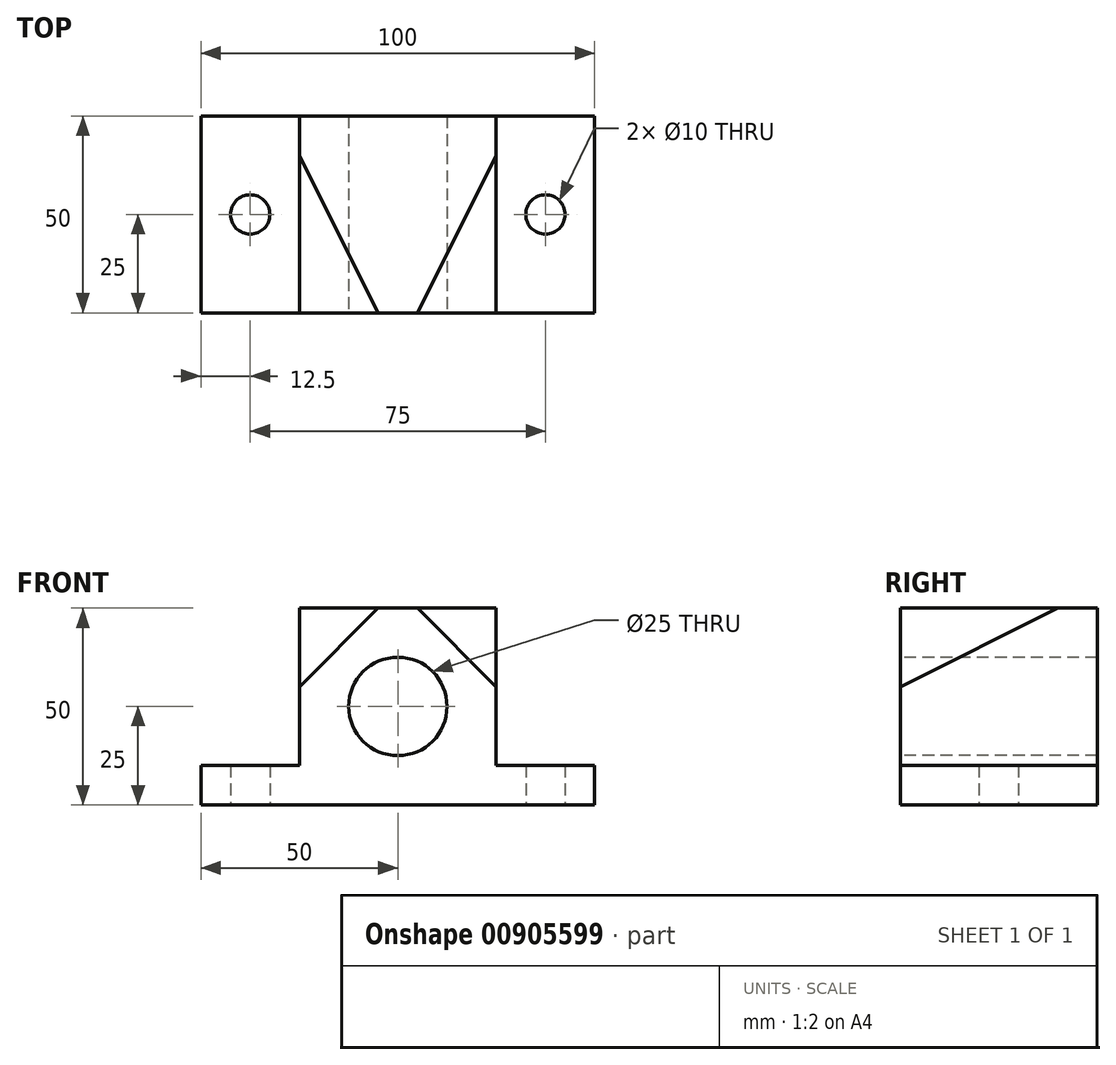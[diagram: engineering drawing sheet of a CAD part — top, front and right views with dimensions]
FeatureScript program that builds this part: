
annotation { "Feature Type Name" : "Feature", "Feature Type Description" : "" }
export const myFeature = defineFeature(function(context is Context, id is Id, definition is map)
    precondition{}
    {
        {
            var Q0;
            Q0=qCreatedBy(makeId("Top.planeOp"),FACE);
            var sketch = newSketch(context, id + "F0", { "sketchPlane" : qUnion([Q0])});
            skLineSegment(sketch, "E0", {"start": v(-73.6, 0) * mm, "end": v(76.3, 0) * mm, "construction": true});
            skLineSegment(sketch, "E1", {"start": v(0, 74.95) * mm, "end": v(0, -74.95) * mm, "construction": true});
            skLineSegment(sketch, "E2.bottom", {"start": v(50, 25) * mm, "end": v(-50, 25) * mm});
            skLineSegment(sketch, "E2.top", {"start": v(50, -25) * mm, "end": v(-50, -25) * mm});
            skLineSegment(sketch, "E2.left", {"start": v(50, 25) * mm, "end": v(50, -25) * mm});
            skLineSegment(sketch, "E2.right", {"start": v(-50, 25) * mm, "end": v(-50, -25) * mm});
            skPoint(sketch, "E2.middle", {"position": v(0, 0) * mm});
            skSolve(sketch);
        }
        {
            var Q0;
            Q0=makeQuery(id+"F0.imprint","IMPRINT",FACE,{"disambiguationData":[TD([[makeQuery(id+"F0.imprint","IMPRINT",EDGE,{"derivedFrom":sQuery(id+"F0.wireOp",EDGE,"E2.bottom")}),1.0]])]});
            extrude(context, id + "F1", {"entities" : qUnion([Q0]), "depth" : 50 * mm, "offsetDistance" : 25 * mm});
        }
        {
            var Q0;
            Q0=makeQuery(id+"F1.opExtrude","SWEPT_FACE",FACE,{"disambiguationData":[OSD([sQuery(id+"F0.wireOp",EDGE,"E2.top")])]});
            var sketch = newSketch(context, id + "F2", { "sketchPlane" : qUnion([Q0])});
            skLineSegment(sketch, "E3.0", {"start": v(-25, 25) * mm, "end": v(25, 25) * mm, "construction": true});
            skLineSegment(sketch, "E3.1", {"start": v(-25, 25) * mm, "end": v(-25, 25) * mm});
            skLineSegment(sketch, "E3.3", {"start": v(25, 25) * mm, "end": v(25, 25) * mm});
            skLineSegment(sketch, "E4", {"start": v(0, 66.46) * mm, "end": v(0, -21.33) * mm, "construction": true});
            skCircle(sketch, "E5", {"center": v(0, 25) * mm, "radius": 12.5 * mm});
            skSolve(sketch);
        }
        {
            var Q0;
            Q0=makeQuery(id+"F2.imprint","IMPRINT",FACE,{"disambiguationData":[TD([[makeQuery(id+"F2.imprint","IMPRINT",EDGE,{"derivedFrom":sQuery(id+"F2.wireOp",EDGE,"E5")}),1.0]])]});
            extrude(context, id + "F3", {"entities" : qUnion([Q0]), "operationType" : NewBodyOperationType.REMOVE, "endBound" : BoundingType.THROUGH_ALL, "oppositeDirection" : true, "depth" : 25 * mm, "offsetDistance" : 25 * mm});
        }
        {
            var Q0;
            Q0=makeQuery(id+"F1.opExtrude","SWEPT_FACE",FACE,{"disambiguationData":[OSD([sQuery(id+"F0.wireOp",EDGE,"E2.top")])]});
            var sketch = newSketch(context, id + "F4", { "sketchPlane" : qUnion([Q0])});
            skLineSegment(sketch, "E6.bottom", {"start": v(-50, 50) * mm, "end": v(-25, 50) * mm});
            skLineSegment(sketch, "E6.top", {"start": v(-50, 10) * mm, "end": v(-25, 10) * mm});
            skLineSegment(sketch, "E6.left", {"start": v(-50, 50) * mm, "end": v(-50, 10) * mm});
            skLineSegment(sketch, "E6.right", {"start": v(-25, 50) * mm, "end": v(-25, 10) * mm});
            skLineSegment(sketch, "E7.MirrorCS", {"start": v(25, 50) * mm, "end": v(25, 10) * mm});
            skLineSegment(sketch, "E8.MirrorCS", {"start": v(50, 50) * mm, "end": v(25, 50) * mm});
            skLineSegment(sketch, "E9.MirrorCS", {"start": v(50, 50) * mm, "end": v(50, 10) * mm});
            skLineSegment(sketch, "E10.MirrorCS", {"start": v(50, 10) * mm, "end": v(25, 10) * mm});
            skSolve(sketch);
        }
        {
            var Q0;
            Q0=makeQuery(id+"F4.imprint","IMPRINT",FACE,{"disambiguationData":[TD([[makeQuery(id+"F4.imprint","IMPRINT",EDGE,{"derivedFrom":sQuery(id+"F4.wireOp",EDGE,"E6.bottom")}),1.0]])]});
            var Q1;
            Q1=makeQuery(id+"F4.imprint","IMPRINT",FACE,{"disambiguationData":[TD([[makeQuery(id+"F4.imprint","IMPRINT",EDGE,{"derivedFrom":sQuery(id+"F4.wireOp",EDGE,"E7.MirrorCS")}),1.0]])]});
            extrude(context, id + "F5", {"entities" : qUnion([Q0, Q1]), "operationType" : NewBodyOperationType.REMOVE, "endBound" : BoundingType.THROUGH_ALL, "oppositeDirection" : true, "depth" : 25 * mm, "offsetDistance" : 25 * mm});
        }
        {
            var Q0;
            Q0=makeQuery(id+"F1.opExtrude","CAP_FACE",FACE,{"disambiguationData":[OSD([sQuery(id+"F0.wireOp",EDGE,"E2.bottom"),sQuery(id+"F0.wireOp",EDGE,"E2.top"),sQuery(id+"F0.wireOp",EDGE,"E2.left"),sQuery(id+"F0.wireOp",EDGE,"E2.right")])],"isStart":true});
            var sketch = newSketch(context, id + "F6", { "sketchPlane" : qUnion([Q0])});
            skLineSegment(sketch, "E11", {"start": v(-73.99, 0) * mm, "end": v(76.67, 0) * mm, "construction": true});
            skPoint(sketch, "E11.endSnap0", {"position": v(50, 0) * mm});
            skLineSegment(sketch, "E12", {"start": v(0, 63.25) * mm, "end": v(0, -70.97) * mm, "construction": true});
            skLineSegment(sketch, "E13.0", {"start": v(-37.5, -25) * mm, "end": v(-37.5, 25) * mm, "construction": true});
            skLineSegment(sketch, "E14.0", {"start": v(37.5, -25) * mm, "end": v(37.5, 25) * mm, "construction": true});
            skCircle(sketch, "E15", {"center": v(-37.5, 0) * mm, "radius": 5 * mm});
            skCircle(sketch, "E16", {"center": v(37.5, 0) * mm, "radius": 5 * mm});
            skSolve(sketch);
        }
        {
            var Q0;
            Q0=makeQuery(id+"F6.imprint","IMPRINT",FACE,{"disambiguationData":[TD([[makeQuery(id+"F6.imprint","IMPRINT",EDGE,{"derivedFrom":sQuery(id+"F6.wireOp",EDGE,"E15")}),1.0]])]});
            var Q1;
            Q1=makeQuery(id+"F6.imprint","IMPRINT",FACE,{"disambiguationData":[TD([[makeQuery(id+"F6.imprint","IMPRINT",EDGE,{"derivedFrom":sQuery(id+"F6.wireOp",EDGE,"E16")}),1.0]])]});
            extrude(context, id + "F7", {"entities" : qUnion([Q0, Q1]), "operationType" : NewBodyOperationType.REMOVE, "endBound" : BoundingType.THROUGH_ALL, "oppositeDirection" : true, "depth" : 25 * mm, "offsetDistance" : 25 * mm});
        }
        {
            var Q0;
            Q0=makeQuery(id+"F1.opExtrude","SWEPT_FACE",FACE,{"disambiguationData":[OSD([sQuery(id+"F0.wireOp",EDGE,"E2.top")])]});
            var sketch = newSketch(context, id + "F8", { "sketchPlane" : qUnion([Q0])});
            skLineSegment(sketch, "E17", {"start": v(5, 50) * mm, "end": v(25, 50) * mm});
            skLineSegment(sketch, "E18", {"start": v(25, 50) * mm, "end": v(25, 30) * mm});
            skLineSegment(sketch, "E19", {"start": v(25, 30) * mm, "end": v(5, 50) * mm});
            skSolve(sketch);
        }
        {
            var Q0;
            Q0=makeQuery(id+"F1.opExtrude","CAP_FACE",FACE,{"disambiguationData":[OSD([sQuery(id+"F0.wireOp",EDGE,"E2.bottom"),sQuery(id+"F0.wireOp",EDGE,"E2.top"),sQuery(id+"F0.wireOp",EDGE,"E2.left"),sQuery(id+"F0.wireOp",EDGE,"E2.right")])],"isStart":false});
            var sketch = newSketch(context, id + "F9", { "sketchPlane" : qUnion([Q0])});
            skLineSegment(sketch, "E20", {"start": v(25, -25) * mm, "end": v(5, -25) * mm});
            skLineSegment(sketch, "E21", {"start": v(5, -25) * mm, "end": v(25, 15) * mm});
            skLineSegment(sketch, "E22", {"start": v(25, 15) * mm, "end": v(25, -25) * mm});
            skSolve(sketch);
        }
        {
            var Q0;
            Q0=sQuery(id+"F8.wireOp",VERTEX,"E17.start");
            var Q1;
            Q1=sQuery(id+"F8.wireOp",VERTEX,"E18.end");
            var Q2;
            Q2=sQuery(id+"F9.wireOp",VERTEX,"E21.end");
            cPlane(context, id + "F10", {"entities" : qUnion([Q0, Q1, Q2]), "cplaneType" : CPlaneType.THREE_POINT, "offset" : 25 * mm, "width" : 150 * mm, "height" : 150 * mm});
        }
        {
            var Q0;
            Q0=qCreatedBy(id+"F10.planeOp",FACE);
            var Q1;
            Q1=sQuery(id+"F8.wireOp",VERTEX,"E17.end");
            cPlane(context, id + "F11", {"entities" : qUnion([Q0, Q1]), "cplaneType" : CPlaneType.PLANE_POINT, "offset" : 25 * mm, "width" : 150 * mm, "height" : 150 * mm});
        }
        {
            var Q0;
            Q0=qCreatedBy(id+"F11.planeOp",FACE);
            var sketch = newSketch(context, id + "F12", { "sketchPlane" : qUnion([Q0])});
            skLineSegment(sketch, "E23.bottom", {"start": v(22.63, 47.37) * mm, "end": v(-40.66, 47.37) * mm});
            skLineSegment(sketch, "E23.top", {"start": v(22.63, -18.36) * mm, "end": v(-40.66, -18.36) * mm});
            skLineSegment(sketch, "E23.left", {"start": v(22.63, 47.37) * mm, "end": v(22.63, -18.36) * mm});
            skLineSegment(sketch, "E23.right", {"start": v(-40.66, 47.37) * mm, "end": v(-40.66, -18.36) * mm});
            skSolve(sketch);
        }
        {
            var Q0;
            Q0=makeQuery(id+"F12.imprint","IMPRINT",FACE,{"disambiguationData":[TD([[makeQuery(id+"F12.imprint","IMPRINT",EDGE,{"derivedFrom":sQuery(id+"F12.wireOp",EDGE,"E23.bottom")}),1.0]])]});
            var Q1;
            Q1=qCreatedBy(id+"F10.planeOp",FACE);
            extrude(context, id + "F13", {"entities" : qUnion([Q0]), "operationType" : NewBodyOperationType.REMOVE, "endBound" : BoundingType.UP_TO_SURFACE, "depth" : 25 * mm, "endBoundEntityFace" : qUnion([Q1]), "offsetDistance" : 25 * mm});
        }
        {
            var Q0;
            Q0=makeQuery(id+"F1.opExtrude","SWEPT_FACE",FACE,{"disambiguationData":[OSD([sQuery(id+"F0.wireOp",EDGE,"E2.top")])]});
            var sketch = newSketch(context, id + "F14", { "sketchPlane" : qUnion([Q0])});
            skLineSegment(sketch, "E24", {"start": v(-25, 50) * mm, "end": v(-25, 30) * mm, "construction": true});
            skLineSegment(sketch, "E25", {"start": v(-25, 30) * mm, "end": v(-5, 50) * mm, "construction": true});
            skLineSegment(sketch, "E26", {"start": v(-5, 50) * mm, "end": v(-25, 50) * mm, "construction": true});
            skSolve(sketch);
        }
        {
            var Q0;
            Q0=makeQuery(id+"F1.opExtrude","CAP_FACE",FACE,{"disambiguationData":[OSD([sQuery(id+"F0.wireOp",EDGE,"E2.bottom"),sQuery(id+"F0.wireOp",EDGE,"E2.top"),sQuery(id+"F0.wireOp",EDGE,"E2.left"),sQuery(id+"F0.wireOp",EDGE,"E2.right")])],"isStart":false});
            var sketch = newSketch(context, id + "F15", { "sketchPlane" : qUnion([Q0])});
            skLineSegment(sketch, "E27", {"start": v(-25, 15) * mm, "end": v(-5, -25) * mm, "construction": true});
            skLineSegment(sketch, "E28", {"start": v(-5, -25) * mm, "end": v(-25, -25) * mm, "construction": true});
            skLineSegment(sketch, "E29", {"start": v(-25, 15) * mm, "end": v(-25, -25) * mm, "construction": true});
            skSolve(sketch);
        }
        {
            var Q0;
            Q0=sQuery(id+"F14.wireOp",VERTEX,"E25.end");
            var Q1;
            Q1=sQuery(id+"F14.wireOp",VERTEX,"E24.end");
            var Q2;
            Q2=sQuery(id+"F15.wireOp",VERTEX,"E27.start");
            cPlane(context, id + "F16", {"entities" : qUnion([Q0, Q1, Q2]), "cplaneType" : CPlaneType.THREE_POINT, "offset" : 25 * mm, "width" : 150 * mm, "height" : 150 * mm});
        }
        {
            var Q0;
            Q0=qCreatedBy(id+"F16.planeOp",FACE);
            cPlane(context, id + "F17", {"entities" : qUnion([Q0]), "cplaneType" : CPlaneType.OFFSET, "offset" : 40 * mm, "width" : 150 * mm, "height" : 150 * mm});
        }
        {
            var Q0;
            Q0=qCreatedBy(id+"F17.planeOp",FACE);
            var sketch = newSketch(context, id + "F18", { "sketchPlane" : qUnion([Q0])});
            skLineSegment(sketch, "E30.bottom", {"start": v(-42.71, -12.34) * mm, "end": v(27.36, -12.34) * mm});
            skLineSegment(sketch, "E30.top", {"start": v(-42.71, 50.33) * mm, "end": v(27.36, 50.33) * mm});
            skLineSegment(sketch, "E30.left", {"start": v(-42.71, -12.34) * mm, "end": v(-42.71, 50.33) * mm});
            skLineSegment(sketch, "E30.right", {"start": v(27.36, -12.34) * mm, "end": v(27.36, 50.33) * mm});
            skSolve(sketch);
        }
        {
            var Q0;
            Q0=makeQuery(id+"F18.imprint","IMPRINT",FACE,{"disambiguationData":[TD([[makeQuery(id+"F18.imprint","IMPRINT",EDGE,{"derivedFrom":sQuery(id+"F18.wireOp",EDGE,"E30.bottom")}),1.0]])]});
            var Q1;
            Q1=qCreatedBy(id+"F16.planeOp",FACE);
            extrude(context, id + "F19", {"entities" : qUnion([Q0]), "operationType" : NewBodyOperationType.REMOVE, "endBound" : BoundingType.UP_TO_SURFACE, "oppositeDirection" : true, "depth" : 25 * mm, "endBoundEntityFace" : qUnion([Q1]), "offsetDistance" : 25 * mm});
        }
    });
